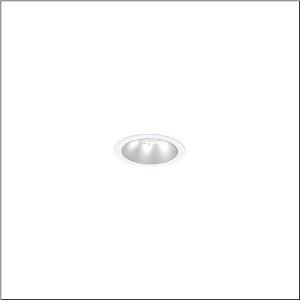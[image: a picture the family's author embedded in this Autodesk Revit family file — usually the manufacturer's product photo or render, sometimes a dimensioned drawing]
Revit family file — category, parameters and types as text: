
# Revit family: lunis_21_s_51db19ta91c
name_source: partatom
category: Lighting Fixtures
units: mm (PartAtom-declared; Revit-internal decimal feet)

## family parameters
Cut with Voids When Loaded = No
Host = Face
Light Source = No
Part Type = Normal
Room Calculation Point = No
Round Connector Dimension = Use Diameter
Shared = No

## types (1)
- --- (1 x LED 3000 K ... 6500 K, 1210 lm, 8 W, 4000K)
    Apparent Load = 8 VA
    CIE Flux Codes = 90 98 100 100 100
    Color Rendering = 80
    Color Temperature = 4000K
    Default Elevation = 1800 mm
    Description = Lunis 21 S, downlight, light control with lens, of PMMA, anti glare with reflector, of plastic, matt, light emission: direct distribution, LED rated luminous flux: 1.200lm, light colour: 8tw, with terminal, 5-pole, mains connection: 220..240V, AC, 50..60Hz, housing, round, of diecast aluminium, traffic white (RAL 9016), diameter: 84mm, clamping range: 1..40mm, protection rating (complete): IP20, protection rating (on room side): IP54, insulation class (complete): insulation class II (safety insulation), certification: CE, impact resistance: IK03, packaging unit: 1 piece
    Height = 0 mm  [stored 0 ft]
    Lamp = 1 x LED 3000 K ... 6500 K
    Lamp Light Flux = 1210 lm
    Lamp Power = 8 W
    Lamp count = 1
    Length = 84 mm
    Luminous efficacy = 151 lm/W
    Manufacturer = Siteco
    ModVariant = No
    Model = 51DB19TA91C
    Mounting Place = Ceiling
    Mounting Type = Recessed
    Number of Poles = 1
    OnlyDefault = Yes
    Power Factor = 1
    Product Name = Lunis 21 S
    Product group = downlight
    ProductGroupID = 401
    Protection Class = Protection class II
    Protection Degree = IP 20
    RLX_Detail_Level = 1
    RLX_Emergency_Light_Flux = 0 lm
    RLX_Emergency_Type = 0
    RLX_Emergency_Type_DB = No
    RlxData = <blob elided: 8713 chars, md5=24d31e79>
    Socket = socket
    Standby Power = 0 W
    System Light Flux = 1210 lm
    System Power = 8 W
    Type Comments = individual setting: CCT=4000K, colour temperature 4000K, luminous flux: 100 % | (OFF | OFF | ON | OFF) | 200 mA
    Type Image = l_1290846.jpg
    URL = http://relux.com
    VarID = @adj_035033
    Voltage = 0 V
    Weight = 0.00 kg
    Width = 0 mm  [stored 0 ft]

note: [stored X ft] marks values corroborated as IEEE doubles in the binary element streams (Revit-internal decimal feet)

## geometry (parser evidence)
native form markers: Sweep x12
no freeform markers — native parametric forms only
